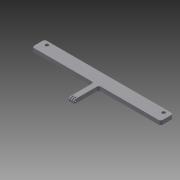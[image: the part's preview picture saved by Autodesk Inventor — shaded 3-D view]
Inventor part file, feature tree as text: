
AUTODESK INVENTOR PART (.ipt)
format: ipt  version: 2015 (Build 190159000, 159)  size: 138,752 bytes
history: native  units: mm
features: extrude x2, fillet x2, sketch x2
ambient origin geometry x8: Origin, YZ Plane, XZ Plane, XY Plane, X Axis, Y Axis, Z Axis, Center Point
bodies: Solid1 (feature_tree)
feature tree (6):
  extrude  "Extrusion1"  Depth=25.0mm
  extrude  "Extrusion3"  Depth=2.0mm
  fillet  "Fillet2"  Radius=3.25mm
  fillet  "Fillet4"  Radius=3.25mm
  sketch  "Sketch1"  dims[d0=254.0mm d1=25.0mm]
  sketch  "Sketch3"  dims[d2=4.0mm d3=8.5mm d4=3.25mm d5=3.25mm d6=4.0mm d7=8.5mm d8=3.25mm d9=3.25mm d13=122.0mm d14=242.25mm d16=2.0mm d17=8.0mm d18=2.0mm d19=8.0mm d20=2.0mm d21=8.0mm d22=2.0mm d23=124.0mm d24=63.0mm d25=8.0mm d26=0.0mm d33=46.75mm d34=0.0mm d36=4.0mm d38=4.0mm d39=2.0mm]
